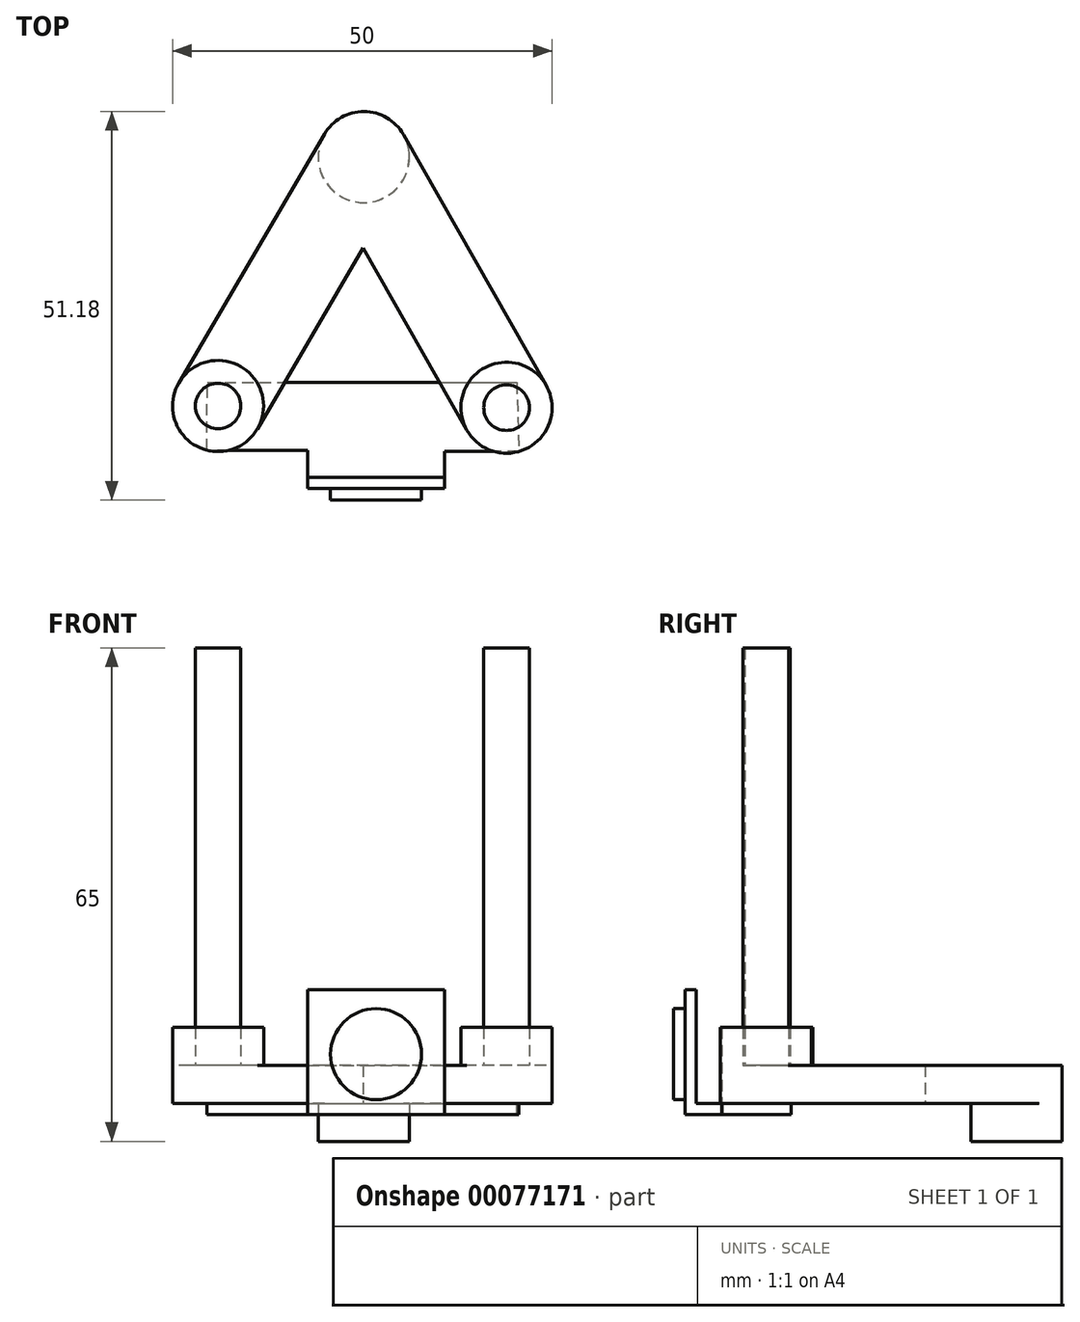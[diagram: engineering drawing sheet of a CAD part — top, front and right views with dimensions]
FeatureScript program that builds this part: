
annotation { "Feature Type Name" : "Feature", "Feature Type Description" : "" }
export const myFeature = defineFeature(function(context is Context, id is Id, definition is map)
    precondition{}
    {
        {
            var Q0;
            Q0=qCreatedBy(makeId("Top.planeOp"),FACE);
            var sketch = newSketch(context, id + "F0", { "sketchPlane" : qUnion([Q0])});
            skLineSegment(sketch, "E0", {"start": v(53.7, 8.74) * mm, "end": v(34.9, 41.76) * mm});
            skLineSegment(sketch, "E1", {"start": v(24.51, 41.83) * mm, "end": v(5.32, 9.03) * mm});
            skCircle(sketch, "E2", {"center": v(29.69, 38.8) * mm, "radius": 6 * mm});
            skCircle(sketch, "E3", {"center": v(10.5, 6) * mm, "radius": 6 * mm});
            skCircle(sketch, "E4", {"center": v(48.5, 5.77) * mm, "radius": 6 * mm});
            skLineSegment(sketch, "E5", {"start": v(15.67, 2.97) * mm, "end": v(29.62, 26.8) * mm});
            skLineSegment(sketch, "E6", {"start": v(29.62, 26.8) * mm, "end": v(43.28, 2.8) * mm});
            skSolve(sketch);
        }
        {
            var Q0;
            Q0=qSketchRegion(id+"F0",true);
            extrude(context, id + "F1", {"entities" : qUnion([Q0]), "depth" : 5 * mm});
        }
        {
            var Q0;
            Q0=makeQuery(id+"F1.opExtrude","CAP_FACE",FACE,{"disambiguationData":[OSD([sQuery(id+"F0.wireOp",EDGE,"E0"),sQuery(id+"F0.wireOp",EDGE,"E1"),sQuery(id+"F0.wireOp",EDGE,"E2"),sQuery(id+"F0.wireOp",EDGE,"E3"),sQuery(id+"F0.wireOp",EDGE,"E4"),sQuery(id+"F0.wireOp",EDGE,"E5"),sQuery(id+"F0.wireOp",EDGE,"E6")])],"isStart":true});
            var sketch = newSketch(context, id + "F2", { "sketchPlane" : qUnion([Q0])});
            skCircle(sketch, "E7", {"center": v(29.69, -38.8) * mm, "radius": 6 * mm});
            skSolve(sketch);
        }
        {
            var Q0;
            Q0=qSketchRegion(id+"F2",true);
            extrude(context, id + "F3", {"entities" : qUnion([Q0]), "operationType" : NewBodyOperationType.ADD, "depth" : 5 * mm});
        }
        {
            var Q0;
            Q0=makeQuery(id+"F1.opExtrude","CAP_FACE",FACE,{"disambiguationData":[OSD([sQuery(id+"F0.wireOp",EDGE,"E0"),sQuery(id+"F0.wireOp",EDGE,"E1"),sQuery(id+"F0.wireOp",EDGE,"E2"),sQuery(id+"F0.wireOp",EDGE,"E3"),sQuery(id+"F0.wireOp",EDGE,"E4"),sQuery(id+"F0.wireOp",EDGE,"E5"),sQuery(id+"F0.wireOp",EDGE,"E6")])],"isStart":false});
            var sketch = newSketch(context, id + "F4", { "sketchPlane" : qUnion([Q0])});
            skCircle(sketch, "E8", {"center": v(10.5, 6) * mm, "radius": 6 * mm});
            skCircle(sketch, "E9", {"center": v(48.5, 5.77) * mm, "radius": 6 * mm});
            skCircle(sketch, "E10", {"center": v(10.5, 6) * mm, "radius": 3 * mm});
            skCircle(sketch, "E11", {"center": v(48.5, 5.77) * mm, "radius": 3 * mm});
            skSolve(sketch);
        }
        {
            var Q0;
            Q0=qSketchRegion(id+"F4",true);
            extrude(context, id + "F5", {"entities" : qUnion([Q0]), "operationType" : NewBodyOperationType.ADD, "depth" : 5 * mm});
        }
        {
            var Q0;
            Q0=makeQuery(id+"F5.opExtrude","CAP_FACE",FACE,{"disambiguationData":[OSD([sQuery(id+"F4.wireOp",EDGE,"E8"),sQuery(id+"F4.wireOp",EDGE,"E10")])],"isStart":false});
            var sketch = newSketch(context, id + "F6", { "sketchPlane" : qUnion([Q0])});
            skCircle(sketch, "E12", {"center": v(10.5, 6) * mm, "radius": 3 * mm});
            skCircle(sketch, "E13", {"center": v(48.5, 5.77) * mm, "radius": 3 * mm});
            skSolve(sketch);
        }
        {
            var Q0;
            Q0=makeQuery(id+"F6.imprint","IMPRINT",FACE,{"disambiguationData":[TD([[makeQuery(id+"F6.imprint","IMPRINT",EDGE,{"derivedFrom":sQuery(id+"F6.wireOp",EDGE,"E13")}),1.0]])]});
            var Q1;
            Q1=makeQuery(id+"F6.imprint","IMPRINT",FACE,{"disambiguationData":[TD([[makeQuery(id+"F6.imprint","IMPRINT",EDGE,{"derivedFrom":sQuery(id+"F6.wireOp",EDGE,"E12")}),1.0]])]});
            extrude(context, id + "F7", {"entities" : qUnion([Q0, Q1]), "depth" : 50 * mm});
        }
        {
            var Q0;
            Q0=makeQuery(id+"F1.opExtrude","CAP_FACE",FACE,{"disambiguationData":[OSD([sQuery(id+"F0.wireOp",EDGE,"E0"),sQuery(id+"F0.wireOp",EDGE,"E1"),sQuery(id+"F0.wireOp",EDGE,"E2"),sQuery(id+"F0.wireOp",EDGE,"E3"),sQuery(id+"F0.wireOp",EDGE,"E4"),sQuery(id+"F0.wireOp",EDGE,"E5"),sQuery(id+"F0.wireOp",EDGE,"E6")])],"isStart":true});
            var sketch = newSketch(context, id + "F8", { "sketchPlane" : qUnion([Q0])});
            skLineSegment(sketch, "E14", {"start": v(50.12, 0) * mm, "end": v(9.03, -0.18) * mm});
            skLineSegment(sketch, "E15", {"start": v(9.03, -0.18) * mm, "end": v(9.07, -9.1) * mm});
            skLineSegment(sketch, "E16", {"start": v(9.07, -9.1) * mm, "end": v(49.84, -9.1) * mm});
            skLineSegment(sketch, "E17", {"start": v(49.84, -9.1) * mm, "end": v(50.12, 0) * mm});
            skSolve(sketch);
        }
        {
            var Q0;
            {var subQ7=sQuery(id+"F8.wireOp",EDGE,"E17");Q0=makeQuery(id+"F8.imprint","IMPRINT",FACE,{"disambiguationData":[TD([[makeQuery(id+"F8.imprint","IMPRINT",EDGE,{"derivedFrom":subQ7}),1.0]])]});}
            var Q1;
            {var subQ7=sQuery(id+"F8.wireOp",EDGE,"E15");Q1=makeQuery(id+"F8.imprint","IMPRINT",FACE,{"disambiguationData":[TD([[makeQuery(id+"F8.imprint","IMPRINT",EDGE,{"derivedFrom":subQ7}),1.0]])]});}
            var Q2;
            {var subQ5=makeQuery(id+"F1.opExtrude","CAP_EDGE",EDGE,{"disambiguationData":[OSD([sQuery(id+"F0.wireOp",EDGE,"E4")])],"isStart":true});var subQ6=sQuery(id+"F8.wireOp",EDGE,"E14");var subQ7=makeQuery(id+"F8.imprint","INTERSECT",VERTEX,{"derivedFrom":[subQ5,subQ6]});Q2=makeQuery(id+"F8.imprint","IMPRINT",FACE,{"disambiguationData":[TD([[makeQuery(id+"F8.imprint","IMPRINT",EDGE,{"disambiguationData":[TD([[subQ7,-1.0]])],"derivedFrom":subQ6}),1.0]])]});}
            extrude(context, id + "F9", {"entities" : qUnion([Q0, Q1, Q2]), "operationType" : NewBodyOperationType.ADD, "depth" : 1.5 * mm});
        }
        {
            var Q0;
            Q0=makeQuery(id+"F9.opExtrude","CAP_FACE",FACE,{"disambiguationData":[OSD([sQuery(id+"F8.wireOp",EDGE,"E14"),sQuery(id+"F8.wireOp",EDGE,"E15"),sQuery(id+"F8.wireOp",EDGE,"E16"),sQuery(id+"F8.wireOp",EDGE,"E17")])],"isStart":false});
            var sketch = newSketch(context, id + "F10", { "sketchPlane" : qUnion([Q0])});
            skLineSegment(sketch, "E18.bottom", {"start": v(22.3, -0.12) * mm, "end": v(40.3, -0.12) * mm});
            skLineSegment(sketch, "E18.top", {"start": v(22.3, 4.88) * mm, "end": v(40.3, 4.88) * mm});
            skLineSegment(sketch, "E18.left", {"start": v(22.3, -0.12) * mm, "end": v(22.3, 4.88) * mm});
            skLineSegment(sketch, "E18.right", {"start": v(40.3, -0.12) * mm, "end": v(40.3, 4.88) * mm});
            skSolve(sketch);
        }
        {
            var Q0;
            Q0=qSketchRegion(id+"F10",true);
            extrude(context, id + "F11", {"entities" : qUnion([Q0]), "operationType" : NewBodyOperationType.ADD, "oppositeDirection" : true, "depth" : 1.5 * mm});
        }
        {
            var Q0;
            Q0=makeQuery(id+"F11.boolean.opBoolean","MERGE",FACE,{"derivedFrom":[makeQuery(id+"F9.opExtrude","CAP_FACE",FACE,{"disambiguationData":[OSD([sQuery(id+"F8.wireOp",EDGE,"E14"),sQuery(id+"F8.wireOp",EDGE,"E15"),sQuery(id+"F8.wireOp",EDGE,"E16"),sQuery(id+"F8.wireOp",EDGE,"E17")])],"isStart":true}),makeQuery(id+"F11.opExtrude","CAP_FACE",FACE,{"disambiguationData":[OSD([sQuery(id+"F10.wireOp",EDGE,"E18.bottom"),sQuery(id+"F10.wireOp",EDGE,"E18.top"),sQuery(id+"F10.wireOp",EDGE,"E18.left"),sQuery(id+"F10.wireOp",EDGE,"E18.right")])],"isStart":false})]});
            var sketch = newSketch(context, id + "F12", { "sketchPlane" : qUnion([Q0])});
            skLineSegment(sketch, "E19.bottom", {"start": v(2577.82, -11.18) * mm, "end": v(2592.82, -11.18) * mm});
            skLineSegment(sketch, "E19.top", {"start": v(2577.82, -9.68) * mm, "end": v(2592.82, -9.68) * mm});
            skLineSegment(sketch, "E19.left", {"start": v(2577.82, -11.18) * mm, "end": v(2577.82, -9.68) * mm});
            skLineSegment(sketch, "E19.right", {"start": v(2592.82, -11.18) * mm, "end": v(2592.82, -9.68) * mm});
            skLineSegment(sketch, "E20.bottom", {"start": v(22.3, -4.88) * mm, "end": v(40.3, -4.88) * mm});
            skLineSegment(sketch, "E20.top", {"start": v(22.3, -3.38) * mm, "end": v(40.3, -3.38) * mm});
            skLineSegment(sketch, "E20.left", {"start": v(22.3, -4.88) * mm, "end": v(22.3, -3.38) * mm});
            skLineSegment(sketch, "E20.right", {"start": v(40.3, -4.88) * mm, "end": v(40.3, -3.38) * mm});
            skSolve(sketch);
        }
        {
            var Q0;
            Q0=qSketchRegion(id+"F12",true);
            extrude(context, id + "F13", {"entities" : qUnion([Q0]), "operationType" : NewBodyOperationType.ADD, "depth" : 15 * mm});
        }
        {
            var Q0;
            Q0=makeQuery(id+"F13.opExtrude","SWEPT_FACE",FACE,{"disambiguationData":[OSD([sQuery(id+"F12.wireOp",EDGE,"E19.bottom")])]});
            var sketch = newSketch(context, id + "F14", { "sketchPlane" : qUnion([Q0])});
            skCircle(sketch, "E21", {"center": v(2585.32, 7.14) * mm, "radius": 5.67 * mm});
            skSolve(sketch);
        }
        {
            var Q0;
            Q0=qSketchRegion(id+"F14",true);
            extrude(context, id + "F15", {"entities" : qUnion([Q0]), "operationType" : NewBodyOperationType.ADD, "depth" : 1 * mm});
        }
        {
            var Q0;
            Q0=makeQuery(id+"F13.boolean.opBoolean","MERGE",FACE,{"derivedFrom":[makeQuery(id+"F11.opExtrude","SWEPT_FACE",FACE,{"disambiguationData":[OSD([sQuery(id+"F10.wireOp",EDGE,"E18.top")])]}),makeQuery(id+"F13.opExtrude","SWEPT_FACE",FACE,{"disambiguationData":[OSD([sQuery(id+"F12.wireOp",EDGE,"E20.bottom")])]})]});
            var sketch = newSketch(context, id + "F16", { "sketchPlane" : qUnion([Q0])});
            skCircle(sketch, "E22", {"center": v(31.3, 6.49) * mm, "radius": 6 * mm});
            skSolve(sketch);
        }
        {
            var Q0;
            Q0=qSketchRegion(id+"F16",true);
            extrude(context, id + "F17", {"entities" : qUnion([Q0]), "operationType" : NewBodyOperationType.ADD, "depth" : 1.5 * mm});
        }
        {
            var Q0;
            Q0=makeQuery(id+"F13.opExtrude","SWEPT_BODY",BODY,{"disambiguationData":[OSD([sQuery(id+"F12.wireOp",EDGE,"E19.bottom"),sQuery(id+"F12.wireOp",EDGE,"E19.top"),sQuery(id+"F12.wireOp",EDGE,"E19.left"),sQuery(id+"F12.wireOp",EDGE,"E19.right")])]});
            var Q1;
            Q1=makeQuery(id+"F15.opExtrude","SWEPT_BODY",BODY,{"disambiguationData":[OSD([sQuery(id+"F14.wireOp",EDGE,"E21")])]});
            deleteBodies(context, id + "F18", {"entities" : qUnion([Q0, Q1])});
        }
    });
